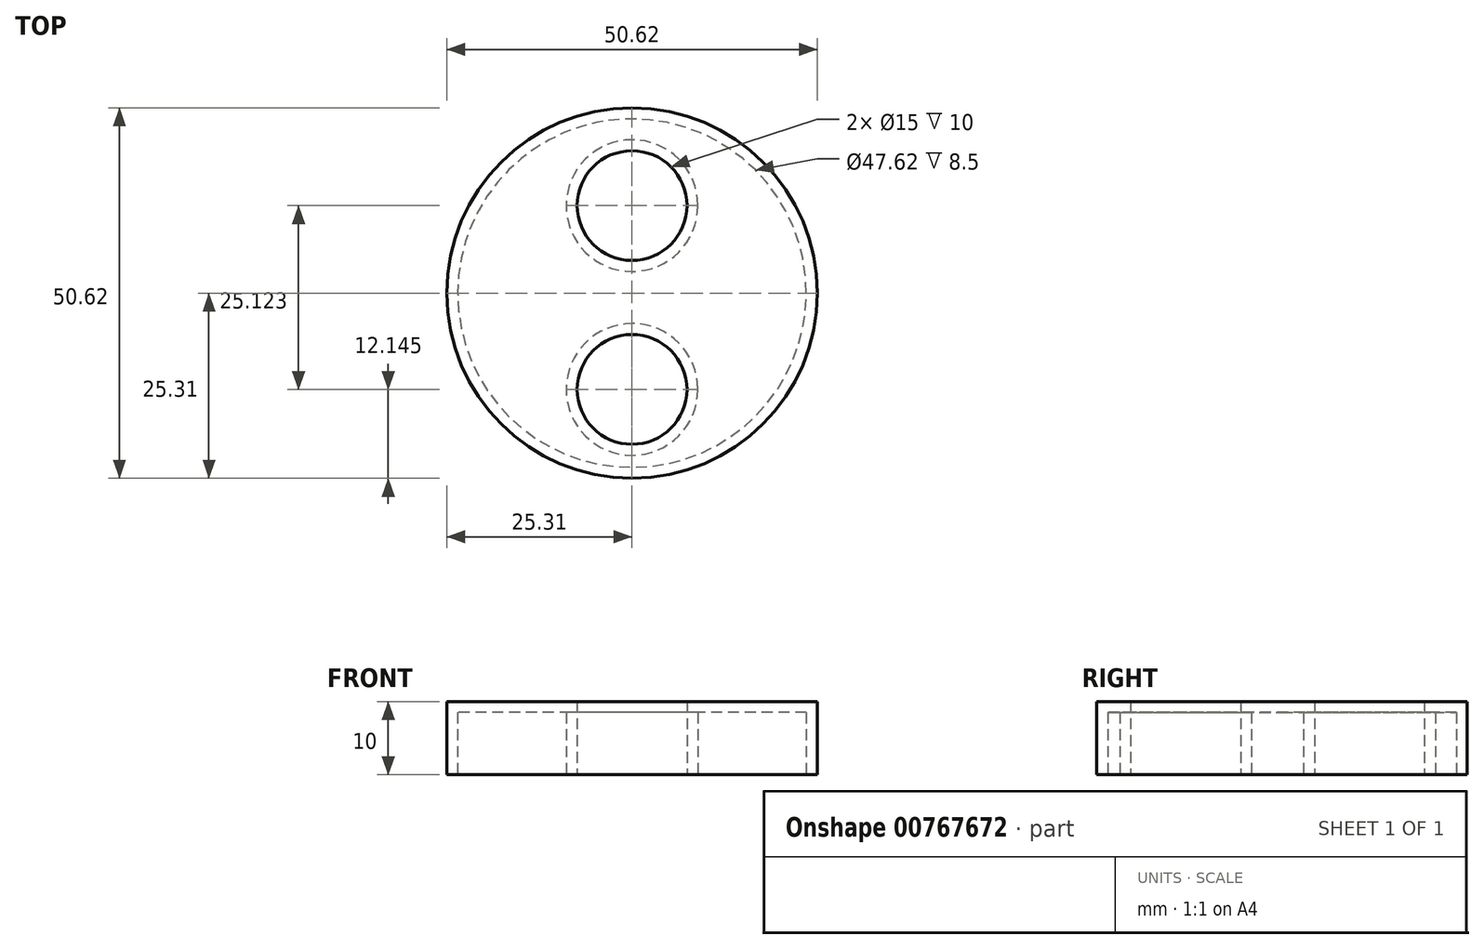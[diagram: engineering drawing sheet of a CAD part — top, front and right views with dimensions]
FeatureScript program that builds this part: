
annotation { "Feature Type Name" : "Feature", "Feature Type Description" : "" }
export const myFeature = defineFeature(function(context is Context, id is Id, definition is map)
    precondition{}
    {
        {
            var Q0;
            Q0=qCreatedBy(makeId("Top.planeOp"),FACE);
            var sketch = newSketch(context, id + "F0", { "sketchPlane" : qUnion([Q0])});
            skCircle(sketch, "E0", {"center": v(0, 0) * mm, "radius": 25.3 * mm});
            skCircle(sketch, "E1", {"center": v(0, -13.17) * mm, "radius": 7.5 * mm});
            skCircle(sketch, "E2", {"center": v(0, 11.96) * mm, "radius": 7.5 * mm});
            skSolve(sketch);
        }
        {
            var Q0;
            Q0=makeQuery(id+"F0.imprint","IMPRINT",FACE,{"disambiguationData":[TD([[makeQuery(id+"F0.imprint","IMPRINT",EDGE,{"derivedFrom":sQuery(id+"F0.wireOp",EDGE,"E0")}),1.0]])]});
            extrude(context, id + "F1", {"entities" : qUnion([Q0]), "depth" : 10 * mm, "offsetDistance" : 25 * mm});
        }
        {
            var Q0;
            Q0=makeQuery(id+"F1.opExtrude","CAP_FACE",FACE,{"disambiguationData":[OSD([sQuery(id+"F0.wireOp",EDGE,"E0"),sQuery(id+"F0.wireOp",EDGE,"E1"),sQuery(id+"F0.wireOp",EDGE,"E2")])],"isStart":true});
            shell(context, id + "F2", {"entities" : qUnion([Q0]), "thickness" : 1.5 * mm});
        }
    });
